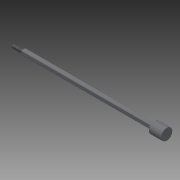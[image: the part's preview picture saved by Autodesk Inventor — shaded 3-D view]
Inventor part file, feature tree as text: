
AUTODESK INVENTOR PART (.ipt)
format: ipt  version: 2013 (Build 170138000, 138)  size: 166,912 bytes
history: native  units: in
note: dims shown in document units (in); Inventor stores cm internally (conversion verified against a paired STEP export)
features: other x119, sketch x4, revolve x3, thread x1, extrude x1
ambient origin geometry x8: Origin, YZ Plane, XZ Plane, XY Plane, X Axis, Y Axis, Z Axis, Center Point
bodies: Solid1 (feature_tree)
feature tree (128):
  revolve  "Revolution1"  Angle=360.0deg
  revolve  "Revolution2"  [1 undecoded]
  thread  "Thread1"  [1 undecoded]
  extrude  "Extrusion1"  [1 undecoded]
  revolve  "Revolution3"  [1 undecoded]
  other  "rod_cp_XY"
  other  "rod_cp_YZ"
  other  "rod_cp_ZX"
  other  "rod_cp_X"
  other  "rod_cp_Y"
  other  "rod_cp_Z"
  other  "rod_cp_Center"
  other  "to_rod_clevis_XY"
  other  "to_rod_clevis_YZ"
  other  "to_rod_clevis_ZX"
  other  "to_rod_clevis_X"
  other  "to_rod_clevis_Y"
  other  "to_rod_clevis_Z"
  other  "to_rod_clevis_Center"
  other  "rl22_XY"
  other  "rl22_YZ"
  other  "rl22_ZX"
  other  "rl22_X"
  other  "rl22_Y"
  other  "rl22_Z"
  other  "rl22_Center"
  other  "rl1_XY"
  other  "rl1_YZ"
  other  "rl1_ZX"
  other  "rl1_X"
  other  "rl1_Y"
  other  "rl1_Z"
  other  "rl1_Center"
  other  "thd1_XY"
  other  "thd1_YZ"
  other  "thd1_ZX"
  other  "thd1_X"
  other  "thd1_Y"
  other  "thd1_Z"
  other  "thd1_Center"
  other  "thd2_XY"
  other  "thd2_YZ"
  other  "thd2_ZX"
  other  "thd2_X"
  other  "thd2_Y"
  other  "thd2_Z"
  other  "thd2_Center"
  other  "dia1_XY"
  other  "dia1_YZ"
  other  "dia1_ZX"
  other  "dia1_X"
  other  "dia1_Y"
  other  "dia1_Z"
  other  "dia1_Center"
  other  "dia2_XY"
  other  "dia2_YZ"
  other  "dia2_ZX"
  other  "dia2_X"
  other  "dia2_Y"
  other  "dia2_Z"
  other  "dia2_Center"
  other  "stroke11_XY"
  other  "stroke11_YZ"
  other  "stroke11_ZX"
  other  "stroke11_X"
  other  "stroke11_Y"
  other  "stroke11_Z"
  other  "stroke11_Center"
  other  "h1_XY"
  other  "h1_YZ"
  other  "h1_ZX"
  other  "h1_X"
  other  "h1_Y"
  other  "h1_Z"
  other  "h1_Center"
  other  "h2_XY"
  other  "h2_YZ"
  other  "h2_ZX"
  other  "h2_X"
  other  "h2_Y"
  other  "h2_Z"
  other  "h2_Center"
  other  "h3_XY"
  other  "h3_YZ"
  other  "h3_ZX"
  other  "h3_X"
  other  "h3_Y"
  other  "h3_Z"
  other  "h3_Center"
  other  "rl2_XY"
  other  "rl2_YZ"
  other  "rl2_ZX"
  other  "rl2_X"
  other  "rl2_Y"
  other  "rl2_Z"
  other  "rl2_Center"
  other  "stroke1_XY"
  other  "stroke1_YZ"
  other  "stroke1_ZX"
  other  "stroke1_X"
  other  "stroke1_Y"
  other  "stroke1_Z"
  other  "stroke1_Center"
  other  "dia12_XY"
  other  "dia12_YZ"
  other  "dia12_ZX"
  other  "dia12_X"
  other  "dia12_Y"
  other  "dia12_Z"
  other  "dia12_Center"
  other  "dia22_XY"
  other  "dia22_YZ"
  other  "dia22_ZX"
  other  "dia22_X"
  other  "dia22_Y"
  other  "dia22_Z"
  other  "dia22_Center"
  other  "stroke1bf_XY"
  other  "stroke1bf_YZ"
  other  "stroke1bf_ZX"
  other  "stroke1bf_X"
  other  "stroke1bf_Y"
  other  "stroke1bf_Z"
  other  "stroke1bf_Center"
  sketch  "Sketch_1"  dims[d0=360.0deg d1=360.0deg]
  sketch  "Sketch_3"  dims[d2=0.4814in d3=0.0in d4=13.312in d5=0.0in d6=360.0deg]
  sketch  "Sketch_31"
  sketch  "Sketch_30"
note: 4 required parameter values undecoded (feature->parameter linkage not recoverable at this tier; creation-order binding heuristic only, values carry confidence <= 0.55)